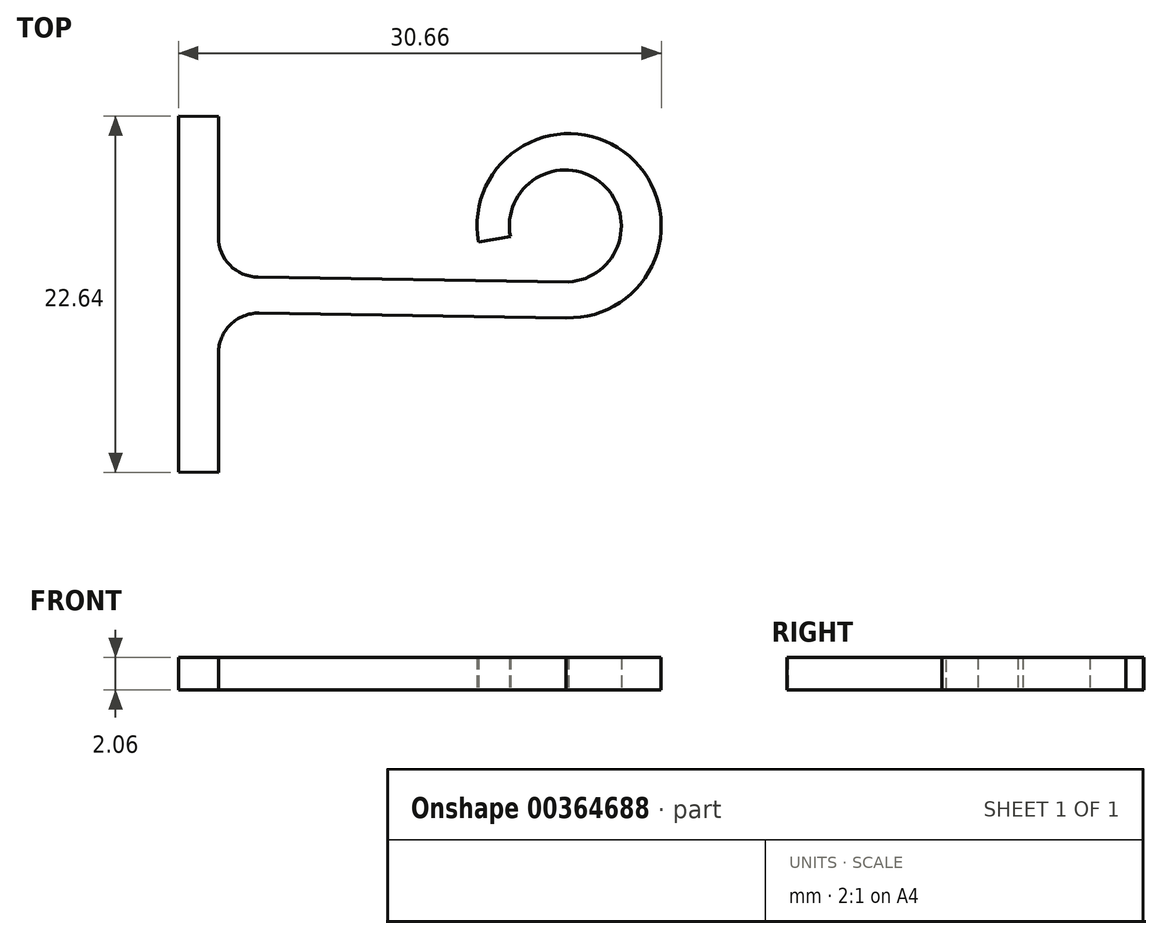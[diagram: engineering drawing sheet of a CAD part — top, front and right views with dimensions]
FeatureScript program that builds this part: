
annotation { "Feature Type Name" : "Feature", "Feature Type Description" : "" }
export const myFeature = defineFeature(function(context is Context, id is Id, definition is map)
    precondition{}
    {
        {
            var Q0;
            Q0=qCreatedBy(makeId("Top.planeOp"),FACE);
            var sketch = newSketch(context, id + "F0", { "sketchPlane" : qUnion([Q0])});
            skPoint(sketch, "E0.centerSnap0", {"position": v(-1.92, -0.73) * mm});
            skPoint(sketch, "E1.centerSnap0", {"position": v(1.9, -0.73) * mm});
            skArc(sketch, "E2", {"start": v(3.03, -7.17) * mm, "mid": v(7.04, 3.1) * mm, "end": v(-2.55, -2.34) * mm});
            skArc(sketch, "E3", {"start": v(3.19, -4.89) * mm, "mid": v(5.16, 1.47) * mm, "end": v(-0.52, -2) * mm});
            skLineSegment(sketch, "E4", {"start": v(-2.55, -2.34) * mm, "end": v(-0.52, -2) * mm});
            skLineSegment(sketch, "E5", {"start": v(3.03, -7.17) * mm, "end": v(-19.05, -6.83) * mm});
            skLineSegment(sketch, "E6", {"start": v(3.19, -4.89) * mm, "end": v(-19.05, -4.55) * mm});
            skPoint(sketch, "E7.end.orphan", {"position": v(-1.5, -6.97) * mm});
            skLineSegment(sketch, "E8", {"start": v(0, 0) * mm, "end": v(0, -12.47) * mm});
            skLineSegment(sketch, "E9.0", {"start": v(-19.05, 5.62) * mm, "end": v(-19.05, -4.55) * mm});
            skPoint(sketch, "E10.orphan", {"position": v(-9.98, -6.97) * mm});
            skLineSegment(sketch, "E11.0", {"start": v(-19.05, 5.62) * mm, "end": v(-21.6, 5.65) * mm});
            skLineSegment(sketch, "E12.0", {"start": v(-19.05, -17) * mm, "end": v(-21.59, -16.95) * mm});
            skLineSegment(sketch, "E13.0", {"start": v(-21.59, 5.65) * mm, "end": v(-21.59, -16.95) * mm});
            skLineSegment(sketch, "E14.trimOffspring", {"start": v(-19.05, -6.83) * mm, "end": v(-19.05, -17) * mm});
            skSolve(sketch);
        }
        {
            var Q0;
            {var subQ0=sQuery(id+"F0.wireOp",EDGE,"E9.0");Q0=makeQuery(id+"F0.imprint","IMPRINT",FACE,{"disambiguationData":[TD([[makeQuery(id+"F0.imprint","IMPRINT",EDGE,{"derivedFrom":subQ0}),-1.0]])]});}
            var Q1;
            {var subQ1=sQuery(id+"F0.wireOp",EDGE,"E2");Q1=makeQuery(id+"F0.imprint","IMPRINT",FACE,{"disambiguationData":[TD([[makeQuery(id+"F0.imprint","IMPRINT",EDGE,{"derivedFrom":subQ1}),1.0]])]});}
            extrude(context, id + "F1", {"entities" : qUnion([Q0, Q1]), "depth" : 2.06 * mm});
        }
        {
            var Q0;
            Q0=makeQuery(id+"F1.opExtrude","SWEPT_EDGE",EDGE,{"disambiguationData":[OSD([sQuery(id+"F0.wireOp",EDGE,"E5"),sQuery(id+"F0.wireOp",EDGE,"E14.trimOffspring")])]});
            var Q1;
            Q1=makeQuery(id+"F1.opExtrude","SWEPT_EDGE",EDGE,{"disambiguationData":[OSD([sQuery(id+"F0.wireOp",EDGE,"E6"),sQuery(id+"F0.wireOp",EDGE,"E9.0")])]});
            fillet(context, id + "F2", {"entities" : qUnion([Q0, Q1]), "radius" : 2.54 * mm, "tangentPropagation" : true, "allowEdgeOverflow" : false});
        }
    });
